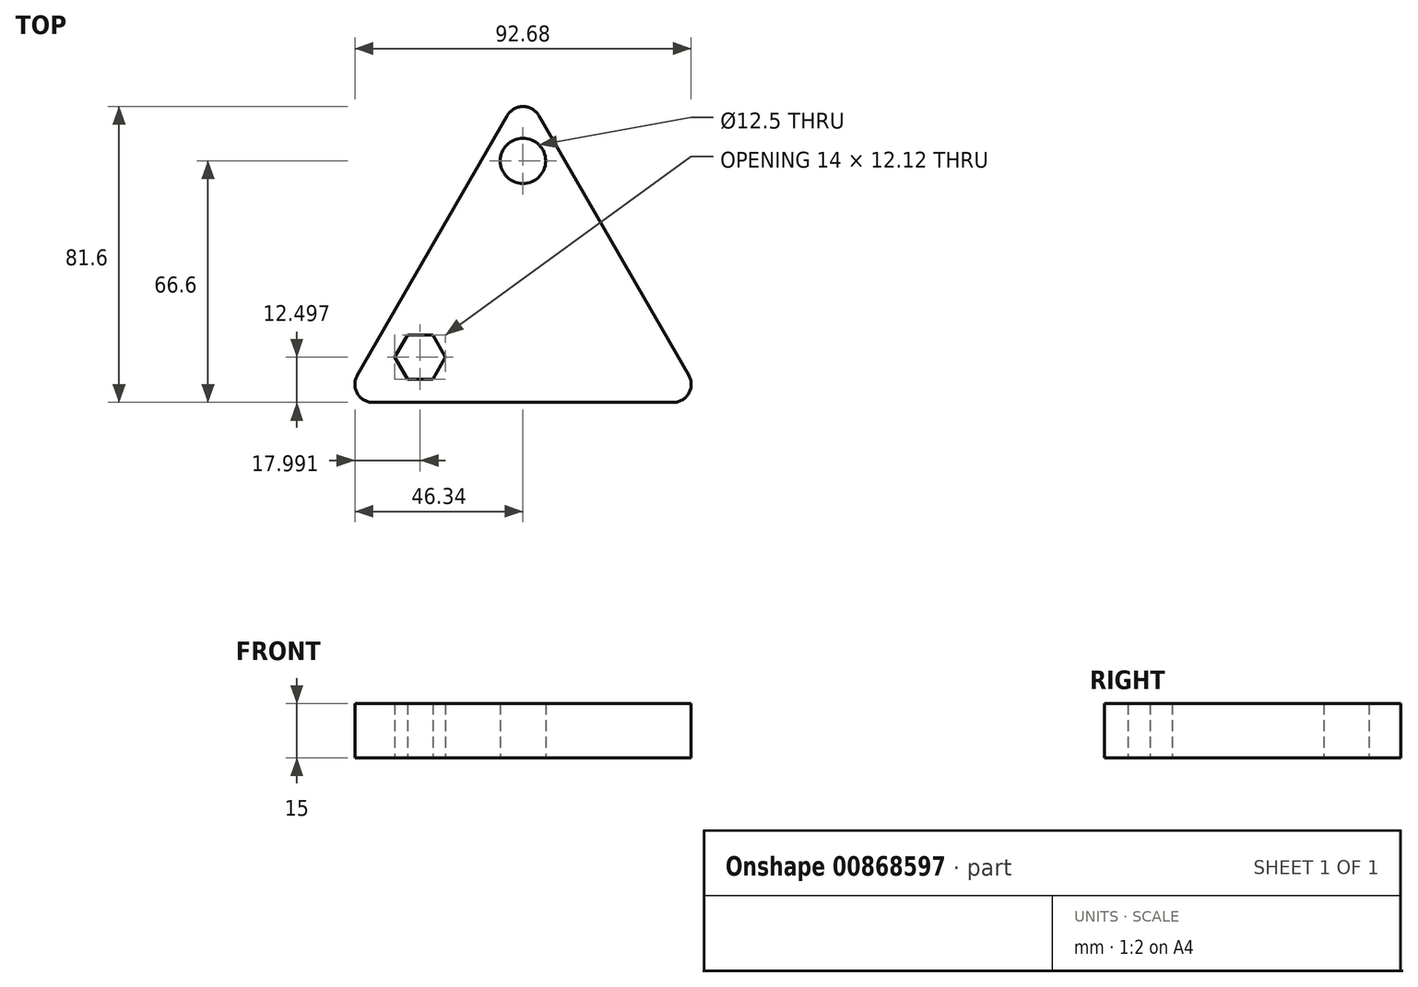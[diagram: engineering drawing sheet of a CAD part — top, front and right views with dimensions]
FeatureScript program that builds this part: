
annotation { "Feature Type Name" : "Feature", "Feature Type Description" : "" }
export const myFeature = defineFeature(function(context is Context, id is Id, definition is map)
    precondition{}
    {
        {
            var Q0;
            Q0=qCreatedBy(makeId("Top.planeOp"),FACE);
            var sketch = newSketch(context, id + "F0", { "sketchPlane" : qUnion([Q0])});
            skLineSegment(sketch, "E0", {"start": v(0, 40) * mm, "end": v(-50, -46.6) * mm});
            skLineSegment(sketch, "E1", {"start": v(-50, -46.6) * mm, "end": v(50, -46.6) * mm});
            skLineSegment(sketch, "E2", {"start": v(50, -46.6) * mm, "end": v(0, 40) * mm});
            skLineSegment(sketch, "E3", {"start": v(0, 0) * mm, "end": v(0, 20) * mm});
            skCircle(sketch, "E4", {"center": v(0, 20) * mm, "radius": 6.25 * mm});
            skLineSegment(sketch, "E5", {"start": v(-50, -46.6) * mm, "end": v(-28.35, -34.1) * mm});
            skCircle(sketch, "E6.cCircle", {"center": v(-28.35, -34.1) * mm, "radius": 6.06 * mm, "construction": true});
            skLineSegment(sketch, "E6.0", {"start": v(-24.85, -28.04) * mm, "end": v(-21.35, -34.1) * mm});
            skLineSegment(sketch, "E6.1", {"start": v(-21.35, -34.1) * mm, "end": v(-24.85, -40.16) * mm});
            skLineSegment(sketch, "E6.2", {"start": v(-24.85, -40.16) * mm, "end": v(-31.85, -40.16) * mm});
            skLineSegment(sketch, "E6.3", {"start": v(-31.85, -40.16) * mm, "end": v(-35.35, -34.1) * mm});
            skLineSegment(sketch, "E6.4", {"start": v(-35.35, -34.1) * mm, "end": v(-31.85, -28.04) * mm});
            skLineSegment(sketch, "E6.5", {"start": v(-31.85, -28.04) * mm, "end": v(-24.85, -28.04) * mm});
            skPoint(sketch, "E6.0.midPoint", {"position": v(-23.1, -31.07) * mm});
            skSolve(sketch);
        }
        {
            var Q0;
            Q0 = qSketchRegion(id + "F0", true);
            extrude(context, id + "F1", {"entities" : qUnion([Q0]), "depth" : 15 * mm, "offsetDistance" : 25 * mm});
        }
        {
            var Q0;
            Q0=makeQuery(id+"F1.opExtrude","SWEPT_EDGE",EDGE,{"disambiguationData":[OSD([sQuery(id+"F0.wireOp",EDGE,"E0"),sQuery(id+"F0.wireOp",EDGE,"E1")])]});
            var Q1;
            Q1=makeQuery(id+"F1.opExtrude","SWEPT_EDGE",EDGE,{"disambiguationData":[OSD([sQuery(id+"F0.wireOp",EDGE,"E1"),sQuery(id+"F0.wireOp",EDGE,"E2")])]});
            var Q2;
            Q2=makeQuery(id+"F1.opExtrude","SWEPT_EDGE",EDGE,{"disambiguationData":[OSD([sQuery(id+"F0.wireOp",EDGE,"E0"),sQuery(id+"F0.wireOp",EDGE,"E2")])]});
            fillet(context, id + "F2", {"entities" : qUnion([Q0, Q1, Q2]), "radius" : 5 * mm, "tangentPropagation" : true, "allowEdgeOverflow" : false});
        }
    });
